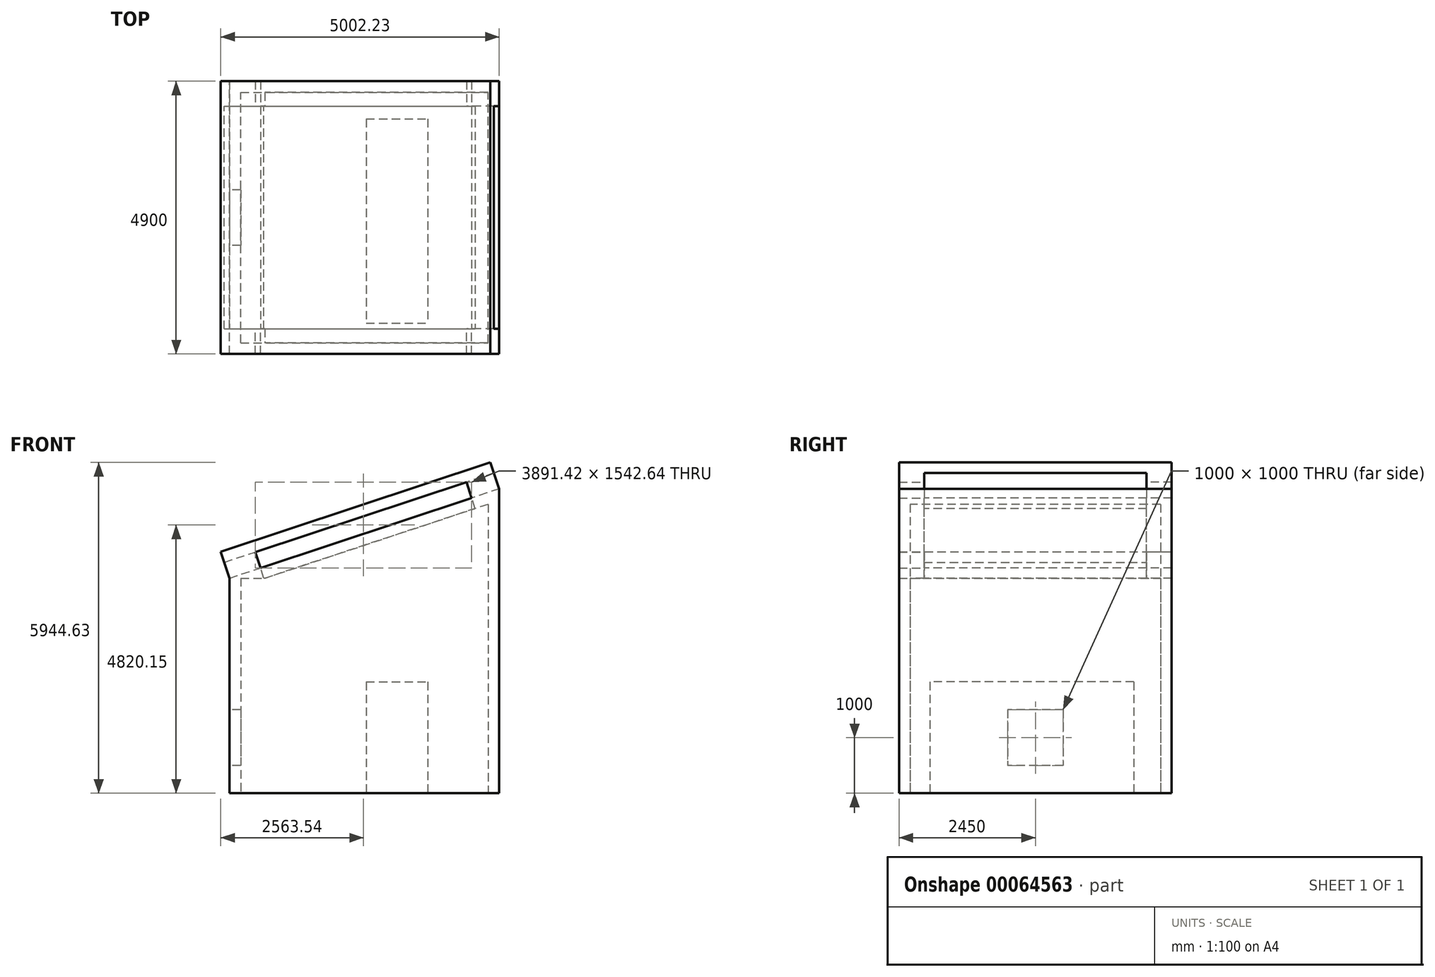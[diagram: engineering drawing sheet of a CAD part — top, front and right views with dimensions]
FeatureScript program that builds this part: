
annotation { "Feature Type Name" : "Feature", "Feature Type Description" : "" }
export const myFeature = defineFeature(function(context is Context, id is Id, definition is map)
    precondition{}
    {
        {
            var Q0;
            Q0=qCreatedBy(makeId("Top.planeOp"),FACE);
            var sketch = newSketch(context, id + "F0", { "sketchPlane" : qUnion([Q0])});
            skLineSegment(sketch, "E0.bottom", {"start": v(0, 0) * mm, "end": v(4845, 0) * mm});
            skLineSegment(sketch, "E0.top", {"start": v(0, 4900) * mm, "end": v(4845, 4900) * mm});
            skLineSegment(sketch, "E0.left", {"start": v(0, 0) * mm, "end": v(0, 4900) * mm});
            skLineSegment(sketch, "E0.right", {"start": v(4845, 0) * mm, "end": v(4845, 4900) * mm});
            skLineSegment(sketch, "E1.0", {"start": v(200, 200) * mm, "end": v(200, 4700) * mm});
            skLineSegment(sketch, "E2.0", {"start": v(200, 4700) * mm, "end": v(4645, 4700) * mm});
            skLineSegment(sketch, "E3.0", {"start": v(4645, 200) * mm, "end": v(4645, 4700) * mm});
            skLineSegment(sketch, "E4.0", {"start": v(200, 200) * mm, "end": v(4645, 200) * mm});
            skLineSegment(sketch, "E5.bottom", {"start": v(2455.65, 4221.4) * mm, "end": v(3563.96, 4221.4) * mm});
            skLineSegment(sketch, "E5.top", {"start": v(2455.65, 555.47) * mm, "end": v(3563.96, 555.47) * mm});
            skLineSegment(sketch, "E5.left", {"start": v(2455.65, 4221.4) * mm, "end": v(2455.65, 555.47) * mm});
            skLineSegment(sketch, "E5.right", {"start": v(3563.96, 4221.4) * mm, "end": v(3563.96, 555.47) * mm});
            skSolve(sketch);
        }
        {
            var Q0;
            Q0=makeQuery(id+"F0.imprint","IMPRINT",FACE,{"disambiguationData":[TD([[makeQuery(id+"F0.imprint","IMPRINT",EDGE,{"derivedFrom":sQuery(id+"F0.wireOp",EDGE,"E0.bottom")}),1.0]])]});
            extrude(context, id + "F1", {"entities" : qUnion([Q0]), "depth" : 3865 * mm});
        }
        {
            var Q0;
            Q0=makeQuery(id+"F1.opExtrude","SWEPT_FACE",FACE,{"disambiguationData":[OSD([sQuery(id+"F0.wireOp",EDGE,"E0.left")])]});
            var sketch = newSketch(context, id + "F2", { "sketchPlane" : qUnion([Q0])});
            skLineSegment(sketch, "E6.bottom", {"start": v(-2950, 1500) * mm, "end": v(-1950, 1500) * mm});
            skLineSegment(sketch, "E6.top", {"start": v(-2950, 500) * mm, "end": v(-1950, 500) * mm});
            skLineSegment(sketch, "E6.left", {"start": v(-2950, 1500) * mm, "end": v(-2950, 500) * mm});
            skLineSegment(sketch, "E6.right", {"start": v(-1950, 1500) * mm, "end": v(-1950, 500) * mm});
            skSolve(sketch);
        }
        {
            var Q0;
            Q0 = qSketchRegion(id + "F2", true);
            extrude(context, id + "F3", {"entities" : qUnion([Q0]), "operationType" : NewBodyOperationType.REMOVE, "oppositeDirection" : true, "depth" : 250 * mm});
        }
        {
            var Q0;
            Q0=makeQuery(id+"F1.opExtrude","SWEPT_FACE",FACE,{"disambiguationData":[OSD([sQuery(id+"F0.wireOp",EDGE,"E0.bottom")])]});
            var sketch = newSketch(context, id + "F4", { "sketchPlane" : qUnion([Q0])});
            skLineSegment(sketch, "E7", {"start": v(0, 3865) * mm, "end": v(4845, 3865) * mm});
            skLineSegment(sketch, "E8", {"start": v(4845, 3865) * mm, "end": v(4845, 5470) * mm});
            skLineSegment(sketch, "E9", {"start": v(4845, 5470) * mm, "end": v(0, 3865) * mm});
            skSolve(sketch);
        }
        {
            var Q0;
            Q0 = qSketchRegion(id + "F4", true);
            extrude(context, id + "F5", {"entities" : qUnion([Q0]), "oppositeDirection" : true, "depth" : 4900 * mm});
        }
        {
            var Q0;
            Q0=makeQuery(id+"F5.opExtrude","SWEPT_FACE",FACE,{"disambiguationData":[OSD([sQuery(id+"F4.wireOp",EDGE,"E7")])]});
            shell(context, id + "F6", {"entities" : qUnion([Q0]), "thickness" : 200 * mm});
        }
        {
            var Q0;
            Q0=makeQuery(id+"F5.opExtrude","SWEPT_FACE",FACE,{"disambiguationData":[OSD([sQuery(id+"F4.wireOp",EDGE,"E9")])]});
            var sketch = newSketch(context, id + "F7", { "sketchPlane" : qUnion([Q0])});
            skLineSegment(sketch, "E10.bottom", {"start": v(1800, 4450) * mm, "end": v(5800, 4450) * mm});
            skLineSegment(sketch, "E10.top", {"start": v(1800, 450) * mm, "end": v(5800, 450) * mm});
            skLineSegment(sketch, "E10.left", {"start": v(1800, 4450) * mm, "end": v(1800, 450) * mm});
            skLineSegment(sketch, "E10.right", {"start": v(5800, 4450) * mm, "end": v(5800, 450) * mm});
            skSolve(sketch);
        }
        {
            var Q0;
            Q0 = qSketchRegion(id + "F7", true);
            extrude(context, id + "F8", {"entities" : qUnion([Q0]), "operationType" : NewBodyOperationType.REMOVE, "oppositeDirection" : true, "depth" : 800 * mm});
        }
        {
            var Q0;
            Q0=makeQuery(id+"F5.opExtrude","SWEPT_FACE",FACE,{"disambiguationData":[OSD([sQuery(id+"F4.wireOp",EDGE,"E9")])]});
            var sketch = newSketch(context, id + "F9", { "sketchPlane" : qUnion([Q0])});
            skLineSegment(sketch, "E11.bottom", {"start": v(1215.4, 4900) * mm, "end": v(1800, 4900) * mm});
            skLineSegment(sketch, "E11.top", {"start": v(1215.4, 4450) * mm, "end": v(1800, 4450) * mm});
            skLineSegment(sketch, "E11.left", {"start": v(1215.4, 4900) * mm, "end": v(1215.4, 4450) * mm});
            skLineSegment(sketch, "E11.right", {"start": v(1800, 4900) * mm, "end": v(1800, 4450) * mm});
            skLineSegment(sketch, "E12.bottom", {"start": v(1215.4, 0) * mm, "end": v(1800, 0) * mm});
            skLineSegment(sketch, "E12.top", {"start": v(1215.4, 450) * mm, "end": v(1800, 450) * mm});
            skLineSegment(sketch, "E12.left", {"start": v(1215.4, 0) * mm, "end": v(1215.4, 450) * mm});
            skLineSegment(sketch, "E12.right", {"start": v(1800, 0) * mm, "end": v(1800, 450) * mm});
            skLineSegment(sketch, "E13.bottom", {"start": v(6319.33, 0) * mm, "end": v(5800, 0) * mm});
            skLineSegment(sketch, "E13.top", {"start": v(6319.33, 450) * mm, "end": v(5800, 450) * mm});
            skLineSegment(sketch, "E13.left", {"start": v(6319.33, 0) * mm, "end": v(6319.33, 450) * mm});
            skLineSegment(sketch, "E13.right", {"start": v(5800, 0) * mm, "end": v(5800, 450) * mm});
            skLineSegment(sketch, "E14.bottom", {"start": v(6319.33, 4900) * mm, "end": v(5800, 4900) * mm});
            skLineSegment(sketch, "E14.top", {"start": v(6319.33, 4450) * mm, "end": v(5800, 4450) * mm});
            skLineSegment(sketch, "E14.left", {"start": v(6319.33, 4900) * mm, "end": v(6319.33, 4450) * mm});
            skLineSegment(sketch, "E14.right", {"start": v(5800, 4900) * mm, "end": v(5800, 4450) * mm});
            skSolve(sketch);
        }
        {
            var Q0;
            Q0 = qSketchRegion(id + "F9", true);
            extrude(context, id + "F10", {"entities" : qUnion([Q0]), "operationType" : NewBodyOperationType.ADD, "depth" : 300 * mm});
        }
        {
            var Q0;
            Q0=makeQuery(id+"F10.opExtrude","CAP_FACE",FACE,{"disambiguationData":[OSD([sQuery(id+"F9.wireOp",EDGE,"E13.bottom"),sQuery(id+"F9.wireOp",EDGE,"E13.top"),sQuery(id+"F9.wireOp",EDGE,"E13.left"),sQuery(id+"F9.wireOp",EDGE,"E13.right")])],"isStart":false});
            var sketch = newSketch(context, id + "F11", { "sketchPlane" : qUnion([Q0])});
            skLineSegment(sketch, "E15.bottom", {"start": v(6319.33, 0) * mm, "end": v(1215.4, 0) * mm});
            skLineSegment(sketch, "E15.top", {"start": v(6319.33, 4900) * mm, "end": v(1215.4, 4900) * mm});
            skLineSegment(sketch, "E15.left", {"start": v(6319.33, 0) * mm, "end": v(6319.33, 4900) * mm});
            skLineSegment(sketch, "E15.right", {"start": v(1215.4, 0) * mm, "end": v(1215.4, 4900) * mm});
            skSolve(sketch);
        }
        {
            var Q0;
            Q0 = qSketchRegion(id + "F11", true);
            extrude(context, id + "F12", {"entities" : qUnion([Q0]), "operationType" : NewBodyOperationType.ADD, "depth" : 200 * mm});
        }
        {
            var Q0;
            Q0=makeQuery(id+"F0.imprint","IMPRINT",FACE,{"disambiguationData":[TD([[makeQuery(id+"F0.imprint","IMPRINT",EDGE,{"derivedFrom":sQuery(id+"F0.wireOp",EDGE,"E5.bottom")}),-1.0]])]});
            extrude(context, id + "F13", {"entities" : qUnion([Q0]), "depth" : 2000 * mm});
        }
    });
